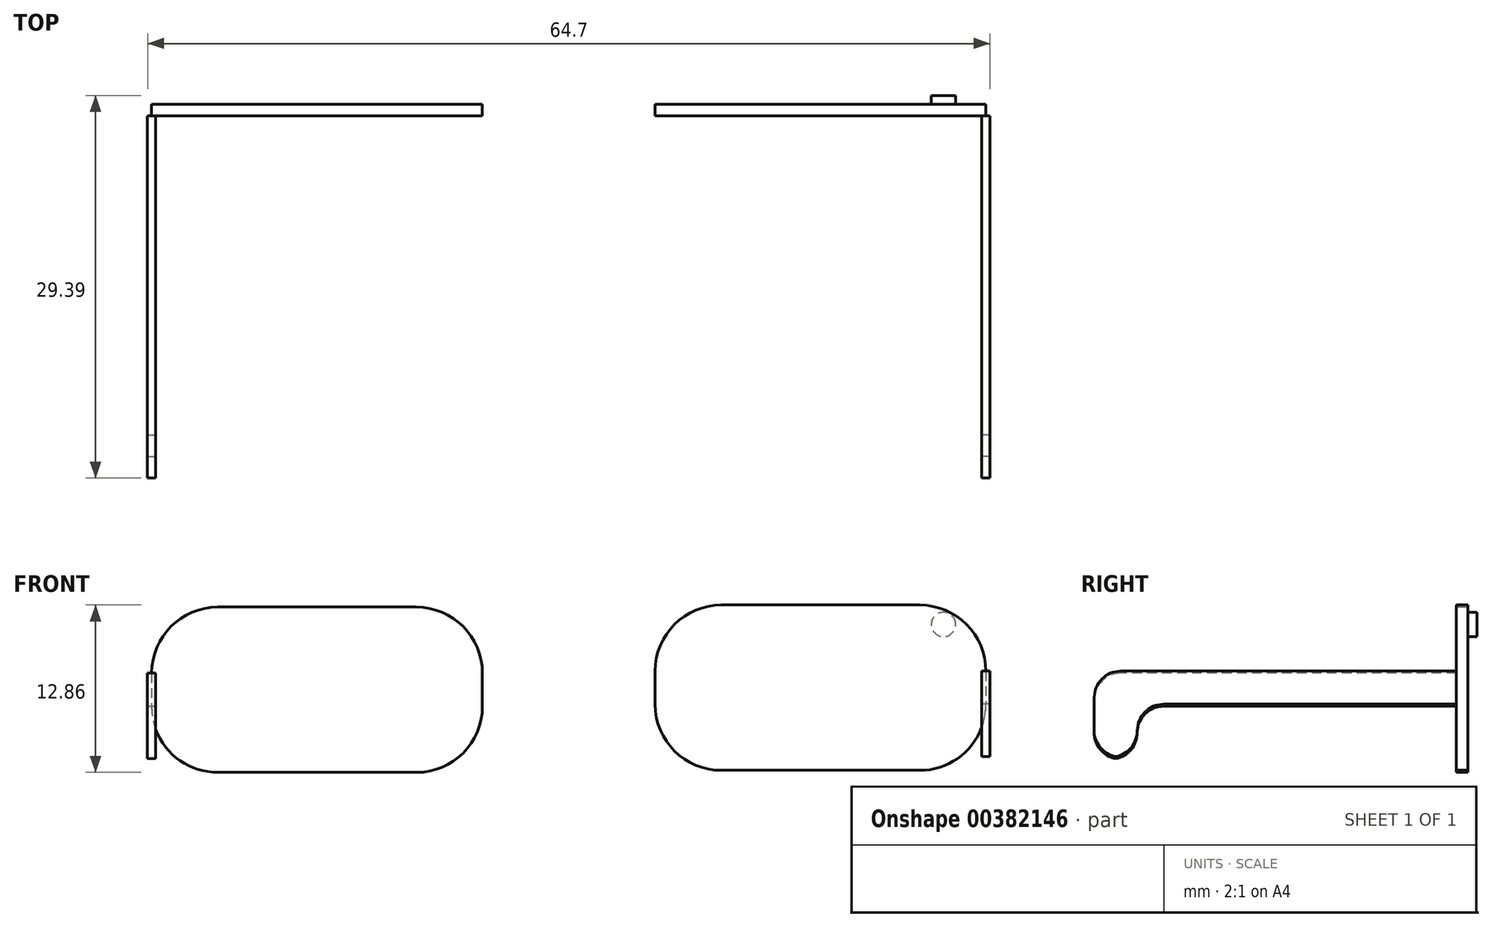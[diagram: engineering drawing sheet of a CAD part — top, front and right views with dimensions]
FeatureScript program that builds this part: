
annotation { "Feature Type Name" : "Feature", "Feature Type Description" : "" }
export const myFeature = defineFeature(function(context is Context, id is Id, definition is map)
    precondition{}
    {
        {
            var Q0;
            Q0=qCreatedBy(makeId("Front.planeOp"),FACE);
            var sketch = newSketch(context, id + "F0", { "sketchPlane" : qUnion([Q0])});
            skLineSegment(sketch, "E0", {"start": v(-38.67, 35.74) * mm, "end": v(-38.67, 23.04) * mm});
            skLineSegment(sketch, "E1", {"start": v(-38.67, 35.74) * mm, "end": v(-13.27, 35.74) * mm});
            skLineSegment(sketch, "E2", {"start": v(-13.27, 35.74) * mm, "end": v(-13.27, 23.04) * mm});
            skLineSegment(sketch, "E3", {"start": v(-38.67, 23.04) * mm, "end": v(-13.27, 23.04) * mm});
            skLineSegment(sketch, "E4", {"start": v(0, 35.9) * mm, "end": v(0, 23.2) * mm});
            skLineSegment(sketch, "E5", {"start": v(0, 35.9) * mm, "end": v(25.4, 35.9) * mm});
            skLineSegment(sketch, "E6", {"start": v(25.4, 35.9) * mm, "end": v(25.4, 23.2) * mm});
            skLineSegment(sketch, "E7", {"start": v(0, 23.2) * mm, "end": v(25.4, 23.2) * mm});
            skSolve(sketch);
        }
        {
            var Q0;
            Q0=makeQuery(id+"F0.imprint","IMPRINT",FACE,{"disambiguationData":[TD([[makeQuery(id+"F0.imprint","IMPRINT",EDGE,{"derivedFrom":sQuery(id+"F0.wireOp",EDGE,"E0")}),1.0]])]});
            var Q1;
            Q1=makeQuery(id+"F0.imprint","IMPRINT",FACE,{"disambiguationData":[TD([[makeQuery(id+"F0.imprint","IMPRINT",EDGE,{"derivedFrom":sQuery(id+"F0.wireOp",EDGE,"E4")}),1.0]])]});
            extrude(context, id + "F1", {"entities" : qUnion([Q0, Q1]), "depth" : 0.89 * mm});
        }
        {
            var Q0;
            Q0=makeQuery(id+"F1.opExtrude","SWEPT_EDGE",EDGE,{"disambiguationData":[OSD([sQuery(id+"F0.wireOp",EDGE,"E0"),sQuery(id+"F0.wireOp",EDGE,"E1")])]});
            var Q1;
            Q1=makeQuery(id+"F1.opExtrude","SWEPT_EDGE",EDGE,{"disambiguationData":[OSD([sQuery(id+"F0.wireOp",EDGE,"E0"),sQuery(id+"F0.wireOp",EDGE,"E3")])]});
            var Q2;
            Q2=makeQuery(id+"F1.opExtrude","SWEPT_EDGE",EDGE,{"disambiguationData":[OSD([sQuery(id+"F0.wireOp",EDGE,"E2"),sQuery(id+"F0.wireOp",EDGE,"E3")])]});
            var Q3;
            Q3=makeQuery(id+"F1.opExtrude","SWEPT_EDGE",EDGE,{"disambiguationData":[OSD([sQuery(id+"F0.wireOp",EDGE,"E1"),sQuery(id+"F0.wireOp",EDGE,"E2")])]});
            var Q4;
            Q4=makeQuery(id+"F1.opExtrude","SWEPT_EDGE",EDGE,{"disambiguationData":[OSD([sQuery(id+"F0.wireOp",EDGE,"E4"),sQuery(id+"F0.wireOp",EDGE,"E5")])]});
            var Q5;
            Q5=makeQuery(id+"F1.opExtrude","SWEPT_EDGE",EDGE,{"disambiguationData":[OSD([sQuery(id+"F0.wireOp",EDGE,"E4"),sQuery(id+"F0.wireOp",EDGE,"E7")])]});
            var Q6;
            Q6=makeQuery(id+"F1.opExtrude","SWEPT_EDGE",EDGE,{"disambiguationData":[OSD([sQuery(id+"F0.wireOp",EDGE,"E6"),sQuery(id+"F0.wireOp",EDGE,"E7")])]});
            var Q7;
            Q7=makeQuery(id+"F1.opExtrude","SWEPT_EDGE",EDGE,{"disambiguationData":[OSD([sQuery(id+"F0.wireOp",EDGE,"E5"),sQuery(id+"F0.wireOp",EDGE,"E6")])]});
            fillet(context, id + "F2", {"entities" : qUnion([Q0, Q1, Q2, Q3, Q4, Q5, Q6, Q7]), "radius" : 5.08 * mm, "tangentPropagation" : true, "allowEdgeOverflow" : false});
        }
        {
            var Q0;
            Q0=makeQuery(id+"F1.opExtrude","CAP_FACE",FACE,{"disambiguationData":[OSD([sQuery(id+"F0.wireOp",EDGE,"E4"),sQuery(id+"F0.wireOp",EDGE,"E5"),sQuery(id+"F0.wireOp",EDGE,"E6"),sQuery(id+"F0.wireOp",EDGE,"E7")])],"isStart":false});
            var sketch = newSketch(context, id + "F3", { "sketchPlane" : qUnion([Q0])});
            skArc(sketch, "E8", {"start": v(0, 30.82) * mm, "mid": v(-6.54, 32.34) * mm, "end": v(-13.1, 30.9) * mm});
            skArc(sketch, "E9", {"start": v(0, 28.28) * mm, "mid": v(-6.6, 30.82) * mm, "end": v(-13.18, 28.28) * mm});
            skLineSegment(sketch, "E10", {"start": v(-17.16, 35.7) * mm, "end": v(5.08, 35.9) * mm});
            skSolve(sketch);
        }
        {
            var Q0;
            Q0=makeQuery(id+"F1.opExtrude","SWEPT_FACE",FACE,{"disambiguationData":[OSD([sQuery(id+"F0.wireOp",EDGE,"E6")])]});
            var sketch = newSketch(context, id + "F4", { "sketchPlane" : qUnion([Q0])});
            skLineSegment(sketch, "E11", {"start": v(0, 30.82) * mm, "end": v(-25.4, 30.82) * mm});
            skLineSegment(sketch, "E12", {"start": v(0, 28.28) * mm, "end": v(-25.4, 28.28) * mm});
            skLineSegment(sketch, "E13", {"start": v(-25.4, 30.82) * mm, "end": v(-28.7, 30.82) * mm});
            skLineSegment(sketch, "E14", {"start": v(-28.7, 30.82) * mm, "end": v(-28.7, 24.21) * mm});
            skLineSegment(sketch, "E15", {"start": v(-28.7, 24.21) * mm, "end": v(-25.4, 24.21) * mm});
            skLineSegment(sketch, "E16", {"start": v(-25.4, 24.21) * mm, "end": v(-25.4, 28.28) * mm});
            skSolve(sketch);
        }
        {
            var Q0;
            {var subQ0=sQuery(id+"F4.wireOp",EDGE,"E13");Q0=makeQuery(id+"F4.imprint","IMPRINT",FACE,{"disambiguationData":[TD([[makeQuery(id+"F4.imprint","IMPRINT",EDGE,{"derivedFrom":subQ0}),1.0]])]});}
            var Q1;
            Q1 = qSketchRegion(id + "F7", true);
            extrude(context, id + "F5", {"entities" : qUnion([Q0, Q1]), "endBound" : BoundingType.SYMMETRIC, "depth" : 0.64 * mm});
        }
        {
            var Q0;
            Q0=makeQuery(id+"F5.opExtrude","SWEPT_EDGE",EDGE,{"disambiguationData":[OSD([sQuery(id+"F4.wireOp",EDGE,"E13"),sQuery(id+"F4.wireOp",EDGE,"E14")])]});
            var Q1;
            Q1=makeQuery(id+"F5.opExtrude","SWEPT_EDGE",EDGE,{"disambiguationData":[OSD([sQuery(id+"F4.wireOp",EDGE,"E14"),sQuery(id+"F4.wireOp",EDGE,"E15")])]});
            var Q2;
            Q2=makeQuery(id+"F5.opExtrude","SWEPT_EDGE",EDGE,{"disambiguationData":[OSD([sQuery(id+"F4.wireOp",EDGE,"E15"),sQuery(id+"F4.wireOp",EDGE,"E16")])]});
            var Q3;
            Q3=makeQuery(id+"F5.opExtrude","SWEPT_EDGE",EDGE,{"disambiguationData":[OSD([sQuery(id+"F4.wireOp",EDGE,"E12"),sQuery(id+"F4.wireOp",EDGE,"E16")])]});
            fillet(context, id + "F6", {"entities" : qUnion([Q0, Q1, Q2, Q3]), "radius" : 2.03 * mm, "tangentPropagation" : true, "allowEdgeOverflow" : false});
        }
        {
            var Q0;
            Q0=makeQuery(id+"F1.opExtrude","SWEPT_FACE",FACE,{"disambiguationData":[OSD([sQuery(id+"F0.wireOp",EDGE,"E0")])]});
            var sketch = newSketch(context, id + "F7", { "sketchPlane" : qUnion([Q0])});
            skLineSegment(sketch, "E17", {"start": v(0, 30.66) * mm, "end": v(25.4, 30.66) * mm});
            skLineSegment(sketch, "E18", {"start": v(0, 28.12) * mm, "end": v(25.4, 28.12) * mm});
            skLineSegment(sketch, "E19", {"start": v(25.4, 30.66) * mm, "end": v(28.7, 30.66) * mm});
            skLineSegment(sketch, "E20", {"start": v(28.7, 30.66) * mm, "end": v(28.7, 24.06) * mm});
            skLineSegment(sketch, "E21", {"start": v(25.4, 28.12) * mm, "end": v(25.4, 24.06) * mm});
            skLineSegment(sketch, "E22", {"start": v(25.4, 24.06) * mm, "end": v(28.7, 24.06) * mm});
            skSolve(sketch);
        }
        {
            var Q0;
            Q0 = qSketchRegion(id + "F7", true);
            var Q1;
            {var subQ0=sQuery(id+"F7.wireOp",EDGE,"E19");Q1=makeQuery(id+"F7.imprint","IMPRINT",FACE,{"disambiguationData":[TD([[makeQuery(id+"F7.imprint","IMPRINT",EDGE,{"derivedFrom":subQ0}),-1.0]])]});}
            extrude(context, id + "F8", {"entities" : qUnion([Q0, Q1]), "endBound" : BoundingType.SYMMETRIC, "depth" : 0.64 * mm});
        }
        {
            var Q0;
            Q0=makeQuery(id+"F8.opExtrude","SWEPT_EDGE",EDGE,{"disambiguationData":[OSD([sQuery(id+"F7.wireOp",EDGE,"E18"),sQuery(id+"F7.wireOp",EDGE,"E21")])]});
            var Q1;
            Q1=makeQuery(id+"F8.opExtrude","SWEPT_EDGE",EDGE,{"disambiguationData":[OSD([sQuery(id+"F7.wireOp",EDGE,"E21"),sQuery(id+"F7.wireOp",EDGE,"E22")])]});
            var Q2;
            Q2=makeQuery(id+"F8.opExtrude","SWEPT_EDGE",EDGE,{"disambiguationData":[OSD([sQuery(id+"F7.wireOp",EDGE,"E20"),sQuery(id+"F7.wireOp",EDGE,"E22")])]});
            var Q3;
            Q3=makeQuery(id+"F8.opExtrude","SWEPT_EDGE",EDGE,{"disambiguationData":[OSD([sQuery(id+"F7.wireOp",EDGE,"E19"),sQuery(id+"F7.wireOp",EDGE,"E20")])]});
            fillet(context, id + "F9", {"entities" : qUnion([Q0, Q1, Q2, Q3]), "radius" : 2.03 * mm, "tangentPropagation" : true, "allowEdgeOverflow" : false});
        }
        {
            var Q0;
            Q0=makeQuery(id+"F1.opExtrude","CAP_FACE",FACE,{"disambiguationData":[OSD([sQuery(id+"F0.wireOp",EDGE,"E4"),sQuery(id+"F0.wireOp",EDGE,"E5"),sQuery(id+"F0.wireOp",EDGE,"E6"),sQuery(id+"F0.wireOp",EDGE,"E7")])],"isStart":true});
            var sketch = newSketch(context, id + "F10", { "sketchPlane" : qUnion([Q0])});
            skCircle(sketch, "E23", {"center": v(-22.14, 34.4) * mm, "radius": 0.94 * mm});
            skCircle(sketch, "E24", {"center": v(-22.14, 34.4) * mm, "radius": 0.64 * mm});
            skCircle(sketch, "E25", {"center": v(-22.14, 34.4) * mm, "radius": 0.4 * mm});
            skSolve(sketch);
        }
        {
            var Q0;
            Q0=makeQuery(id+"F10.imprint","IMPRINT",FACE,{"disambiguationData":[TD([[makeQuery(id+"F10.imprint","IMPRINT",EDGE,{"derivedFrom":sQuery(id+"F10.wireOp",EDGE,"E25")}),1.0]])]});
            var Q1;
            Q1=makeQuery(id+"F10.imprint","IMPRINT",FACE,{"disambiguationData":[TD([[makeQuery(id+"F10.imprint","IMPRINT",EDGE,{"derivedFrom":sQuery(id+"F10.wireOp",EDGE,"E24")}),1.0]])]});
            var Q2;
            Q2=makeQuery(id+"F10.imprint","IMPRINT",FACE,{"disambiguationData":[TD([[makeQuery(id+"F10.imprint","IMPRINT",EDGE,{"derivedFrom":sQuery(id+"F10.wireOp",EDGE,"E23")}),1.0]])]});
            extrude(context, id + "F11", {"entities" : qUnion([Q0, Q1, Q2]), "operationType" : NewBodyOperationType.ADD, "depth" : 0.69 * mm});
        }
        {
            var Q0;
            Q0=sQuery(id+"F3.wireOp",EDGE,"E10");
            var Q1;
            Q1=sQuery(id+"F3.wireOp",EDGE,"E8");
            var Q2;
            Q2=sQuery(id+"F3.wireOp",EDGE,"E9");
            extrude(context, id + "F12", {"bodyType" : ToolBodyType.SURFACE, "surfaceEntities" : qUnion([Q0, Q1, Q2]), "endBound" : BoundingType.SYMMETRIC, "depth" : 0.06 * mm});
        }
    });
